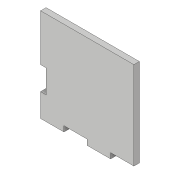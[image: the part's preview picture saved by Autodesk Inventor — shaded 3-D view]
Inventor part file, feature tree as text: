
AUTODESK INVENTOR PART (.ipt)
format: ipt  version: 2017 (Build 210142000, 142)  size: 94,208 bytes
history: native  units: in
note: dims shown in document units (in); Inventor stores cm internally (conversion verified against a paired STEP export)
features: extrude x2, sketch x2
ambient origin geometry x8: Origin, YZ Plane, XZ Plane, XY Plane, X Axis, Y Axis, Z Axis, Center Point
bodies: Solid1 (feature_tree)
feature tree (4):
  extrude  "Extrusion1"  Depth=2.0in
  extrude  "Extrusion2"  Depth=0.5in
  sketch  "Sketch1"  dims[d0=2.0in d1=2.0in]
  sketch  "Sketch2"  dims[d2=0.117in d3=0.0in d4=0.5in d5=0.117in d6=0.5in d7=0.117in d8=0.117in d9=0.5in d10=0.5in d11=0.117in d12=0.0in]
